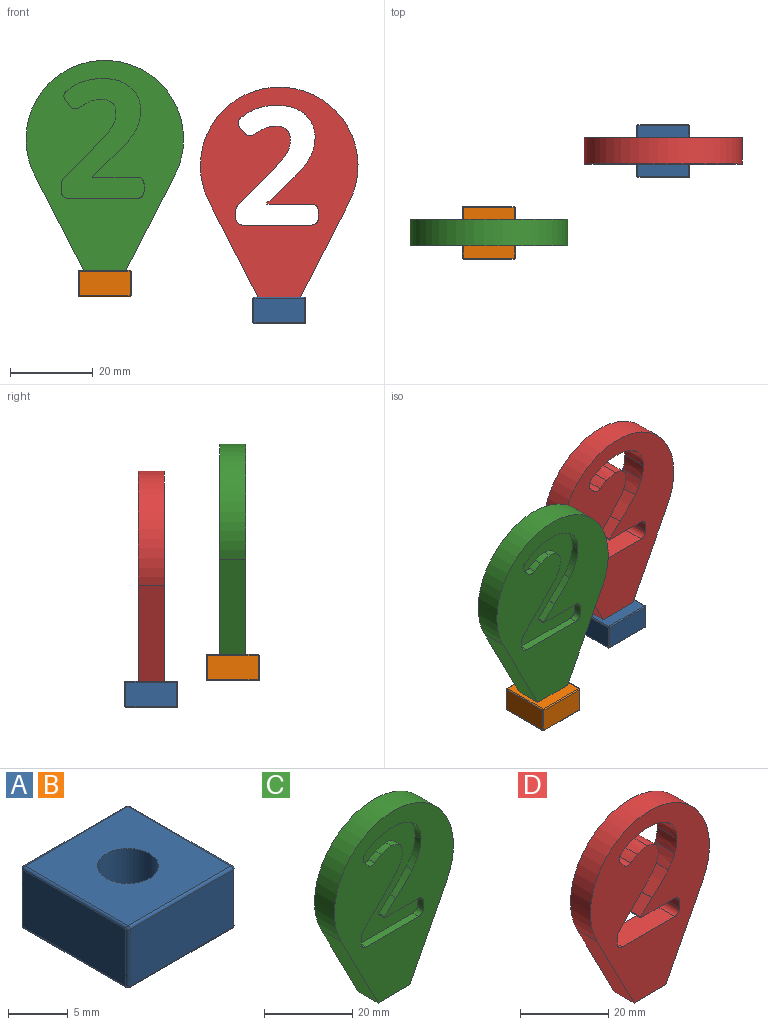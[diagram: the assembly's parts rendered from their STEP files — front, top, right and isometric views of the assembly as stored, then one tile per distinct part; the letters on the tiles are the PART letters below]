
ASSEMBLY  parts=4 mates=2
PART A: 28 faces, bbox 12.7x12.7x6.4 mm
  f0: plane 12.19x5.84mm, normal (-1,0,0), area 71.2mm2, adj f16,f21,f24,f27
  f1: plane 12.19x5.84mm, normal (0,-1,0), area 71.2mm2, adj f13,f22,f23,f27
  f2: plane 12.19x5.84mm, normal (1,0,0), area 71.2mm2, adj f8,f12,f13,f14
  f3: cylinder r=2.54mm len=5.08mm, axis (0,0,-1), area 60.8mm2, adj f5,f7
  f4: plane 12.19x5.84mm, normal (0,1,0), area 71.2mm2, adj f8,f11,f15,f16
  f5: plane 12.19x12.19mm, normal (0,0,1), area 128.4mm2, adj f3,f11,f12,f21,f22
  f6: plane 12.19x12.19mm, normal (0,0,-1), area 67.6mm2, adj f7,f14,f15,f23,f24
  f7: cone r=5.08mm half-angle=45deg, axis (0,0,-1), area 86mm2, adj f3,f6
  f8: cylinder r=0.25mm len=5.84mm, axis (0,0,-1), area 2.3mm2, adj f2,f4,f9,f10
  f9: sphere r=0.25mm, area 0.1mm2, adj f8,f11,f12
  f10: sphere r=0.25mm, area 0.1mm2, adj f8,f14,f15
  f11: cylinder r=0.25mm len=12.19mm, axis (1,0,0), area 4.9mm2, adj f4,f5,f9,f17
  f12: cylinder r=0.25mm len=12.19mm, axis (0,-1,0), area 4.9mm2, adj f2,f5,f9,f18
  f13: cylinder r=0.25mm len=5.84mm, axis (0,0,1), area 2.3mm2, adj f1,f2,f18,f19
  f14: cylinder r=0.25mm len=12.19mm, axis (0,1,0), area 4.9mm2, adj f2,f6,f10,f19
  f15: cylinder r=0.25mm len=12.19mm, axis (-1,0,0), area 4.9mm2, adj f4,f6,f10,f20
  f16: cylinder r=0.25mm len=5.84mm, axis (0,0,1), area 2.3mm2, adj f0,f4,f17,f20
  f17: sphere r=0.25mm, area 0.1mm2, adj f11,f16,f21
  f18: sphere r=0.25mm, area 0.1mm2, adj f12,f13,f22
  f19: sphere r=0.25mm, area 0.1mm2, adj f13,f14,f23
  f20: sphere r=0.25mm, area 0.1mm2, adj f15,f16,f24
  f21: cylinder r=0.25mm len=12.19mm, axis (0,1,0), area 4.9mm2, adj f0,f5,f17,f25
  f22: cylinder r=0.25mm len=12.19mm, axis (-1,0,0), area 4.9mm2, adj f1,f5,f18,f25
  f23: cylinder r=0.25mm len=12.19mm, axis (1,0,0), area 4.9mm2, adj f1,f6,f19,f26
  f24: cylinder r=0.25mm len=12.19mm, axis (0,-1,0), area 4.9mm2, adj f0,f6,f20,f26
  f25: sphere r=0.25mm, area 0.1mm2, adj f21,f22,f27
  f26: sphere r=0.25mm, area 0.1mm2, adj f23,f24,f27
  f27: cylinder r=0.25mm len=5.84mm, axis (0,0,-1), area 2.3mm2, adj f0,f1,f25,f26
PART B: same geometry as A
PART C: 70 faces, bbox 38.1x6.4x50.8 mm
  f0: plane 1.91x1.9mm, normal (-1,0,0), area 3.6mm2, adj f30,f31,f61,f68
  f1: plane 16.78x1.91mm, normal (0,0,1), area 32mm2, adj f24,f31,f61,f68
  f2: plane 1.96x1.91mm, normal (1,0,0), area 3.7mm2, adj f24,f25,f61,f68
  f3: plane 6.78x6.71mm, normal (0.71,0,-0.7), area 18.2mm2, adj f19,f25,f61,f68
  f4: extruded ~2.33x1.91mm, area 5.2mm2, adj f5,f19,f61,f68
  f5: extruded ~2.22x1.91mm, area 4.3mm2, adj f4,f6,f61,f68
  f6: extruded ~2.56x1.91mm, area 5.4mm2, adj f5,f7,f61,f68
  f7: extruded ~2.53x1.91mm, area 5.2mm2, adj f6,f8,f61,f68
  f8: extruded ~3.22x1.91mm, area 6.4mm2, adj f7,f20,f61,f68
  f9: plane 1.91x1.49mm, normal (0.76,0,0.65), area 3.7mm2, adj f26,f27,f61,f68
  f10: extruded ~3.03x1.91mm, area 6.2mm2, adj f11,f21,f61,f68
  f11: extruded ~3.67x1.91mm, area 7mm2, adj f10,f12,f61,f68
  f12: extruded ~4.72x1.91mm, area 9.3mm2, adj f11,f13,f61,f68
  f13: extruded ~3.18x2.73mm, area 8.1mm2, adj f12,f14,f61,f68
  f14: extruded ~4.02x1.91mm, area 8.1mm2, adj f13,f15,f61,f68
  f15: extruded ~3.7x1.91mm, area 7.2mm2, adj f14,f16,f61,f68
  f16: extruded ~3.54x2.15mm, area 7.9mm2, adj f15,f22,f61,f68
  f17: plane 3.67x3.45mm, normal (-0.69,0,0.73), area 9.6mm2, adj f23,f28,f61,f68
  f18: plane 10.85x1.91mm, normal (0,0,-1), area 20.7mm2, adj f23,f30,f61,f68
  f19: extruded ~4.52x4.16mm, area 11.7mm2, adj f3,f4,f61,f68
  f20: extruded ~2.1x1.91mm, area 4.7mm2, adj f8,f26,f61,f68
  f21: extruded ~2.22x1.91mm, area 5.1mm2, adj f10,f27,f61,f68
  f22: extruded ~5.17x5.12mm, area 13.9mm2, adj f16,f28,f61,f68
  f23: plane 1.91x0.27mm, normal (-1,0,0), area 0.5mm2, adj f17,f18,f61,f68
  f24: cylinder r=1.59mm len=1.91mm, axis (0,-1,0), area 4.8mm2, adj f1,f2,f61,f68
  f25: cylinder r=1.59mm len=1.91mm, axis (0,-1,0), area 2.4mm2, adj f2,f3,f61,f68
  f26: cylinder r=1.59mm len=2.14mm, axis (0,1,0), area 4.5mm2, adj f9,f20,f61,f68
  f27: cylinder r=1.59mm len=2.28mm, axis (0,1,0), area 4.9mm2, adj f9,f21,f61,f68
  f28: cylinder r=1.59mm len=1.91mm, axis (0,1,0), area 0mm2, adj f17,f22,f61,f68
  f29: cylinder r=1.59mm len=1.91mm, axis (0,1,0), area 0mm2, adj f55,f56,f60,f69
  f30: cylinder r=1.59mm len=1.91mm, axis (0,-1,0), area 4.8mm2, adj f0,f18,f61,f68
  f31: cylinder r=1.59mm len=1.91mm, axis (0,-1,0), area 4.8mm2, adj f0,f1,f61,f68
  f32: cylinder r=19.05mm len=38.1mm, axis (0,1,0), area 495.1mm2, adj f33,f59,f60,f61
  f33: plane 23.03x11.86mm, normal (-0.89,0,-0.46), area 164.5mm2, adj f32,f34,f60,f61
  f34: plane 10.16x6.35mm, normal (0,0,-1), area 64.5mm2, adj f33,f59,f60,f61
  f35: plane 1.91x1.9mm, normal (-1,0,0), area 3.6mm2, adj f60,f66,f67,f69
  f36: plane 16.78x1.91mm, normal (0,0,1), area 32mm2, adj f60,f62,f67,f69
  f37: plane 1.96x1.91mm, normal (1,0,0), area 3.7mm2, adj f60,f62,f63,f69
  f38: plane 6.78x6.71mm, normal (0.71,0,-0.7), area 18.2mm2, adj f39,f60,f63,f69
  f39: extruded ~4.52x4.16mm, area 11.7mm2, adj f38,f40,f60,f69
  f40: extruded ~2.33x1.91mm, area 5.2mm2, adj f39,f41,f60,f69
  f41: extruded ~2.22x1.91mm, area 4.3mm2, adj f40,f42,f60,f69
  f42: extruded ~2.56x1.91mm, area 5.4mm2, adj f41,f43,f60,f69
  f43: extruded ~2.53x1.91mm, area 5.2mm2, adj f42,f44,f60,f69
  f44: extruded ~3.22x1.91mm, area 6.4mm2, adj f43,f45,f60,f69
  f45: extruded ~2.1x1.91mm, area 4.7mm2, adj f44,f60,f64,f69
  f46: plane 1.91x1.49mm, normal (0.76,0,0.65), area 3.7mm2, adj f60,f64,f65,f69
  f47: extruded ~2.22x1.91mm, area 5.1mm2, adj f48,f60,f65,f69
  f48: extruded ~3.03x1.91mm, area 6.2mm2, adj f47,f49,f60,f69
  f49: extruded ~3.67x1.91mm, area 7mm2, adj f48,f50,f60,f69
  f50: extruded ~4.72x1.91mm, area 9.3mm2, adj f49,f51,f60,f69
  f51: extruded ~3.18x2.73mm, area 8.1mm2, adj f50,f52,f60,f69
  f52: extruded ~4.02x1.91mm, area 8.1mm2, adj f51,f53,f60,f69
  f53: extruded ~3.7x1.91mm, area 7.2mm2, adj f52,f54,f60,f69
  f54: extruded ~3.54x2.15mm, area 7.9mm2, adj f53,f55,f60,f69
  f55: extruded ~5.17x5.12mm, area 13.9mm2, adj f29,f54,f60,f69
  f56: plane 3.67x3.45mm, normal (-0.69,0,0.73), area 9.6mm2, adj f29,f57,f60,f69
  f57: plane 1.91x0.27mm, normal (-1,0,0), area 0.5mm2, adj f56,f58,f60,f69
  f58: plane 10.85x1.91mm, normal (0,0,-1), area 20.7mm2, adj f57,f60,f66,f69
  f59: plane 23.03x11.86mm, normal (0.89,0,-0.46), area 164.5mm2, adj f32,f34,f60,f61
  f60: plane 50.8x38.1mm, normal (0,-1,0), area 1096.6mm2, adj f29,f32,f33,f34,f35,f36,f37,f38
  f61: plane 50.8x38.1mm, normal (0,1,0), area 1096.6mm2, adj f0,f1,f2,f3,f4,f5,f6,f7
  f62: cylinder r=1.59mm len=1.91mm, axis (0,-1,0), area 4.8mm2, adj f36,f37,f60,f69
  f63: cylinder r=1.59mm len=1.91mm, axis (0,-1,0), area 2.4mm2, adj f37,f38,f60,f69
  f64: cylinder r=1.59mm len=2.14mm, axis (0,1,0), area 4.5mm2, adj f45,f46,f60,f69
  f65: cylinder r=1.59mm len=2.28mm, axis (0,1,0), area 4.9mm2, adj f46,f47,f60,f69
  f66: cylinder r=1.59mm len=1.91mm, axis (0,-1,0), area 4.8mm2, adj f35,f58,f60,f69
  f67: cylinder r=1.59mm len=1.91mm, axis (0,-1,0), area 4.8mm2, adj f35,f36,f60,f69
  f68: plane 28.95x19.95mm, normal (0,1,0), area 300.7mm2, adj f0,f1,f2,f3,f4,f5,f6,f7
  f69: plane 28.95x19.95mm, normal (0,-1,0), area 300.7mm2, adj f29,f35,f36,f37,f38,f39,f40,f41
PART D: 37 faces, bbox 38.1x6.4x50.8 mm
  f0: cylinder r=19.05mm len=38.1mm, axis (0,1,0), area 495.1mm2, adj f1,f27,f28,f29
  f1: plane 23.03x11.86mm, normal (-0.89,0,-0.46), area 164.5mm2, adj f0,f2,f28,f29
  f2: plane 10.16x6.35mm, normal (0,0,-1), area 64.5mm2, adj f1,f27,f28,f29
  f3: plane 6.35x1.9mm, normal (-1,0,0), area 12.1mm2, adj f28,f29,f35,f36
  f4: plane 16.78x6.35mm, normal (0,0,1), area 106.5mm2, adj f28,f29,f30,f36
  f5: plane 6.35x1.96mm, normal (1,0,0), area 12.4mm2, adj f28,f29,f30,f31
  f6: plane 6.78x6.71mm, normal (0.71,0,-0.7), area 60.5mm2, adj f7,f28,f29,f31
  f7: extruded ~6.35x4.52mm, area 39mm2, adj f6,f8,f28,f29
  f8: extruded ~6.35x2.33mm, area 17.4mm2, adj f7,f9,f28,f29
  f9: extruded ~6.35x2.22mm, area 14.5mm2, adj f8,f10,f28,f29
  f10: extruded ~6.35x2.56mm, area 17.9mm2, adj f9,f11,f28,f29
  f11: extruded ~6.35x2.53mm, area 17.3mm2, adj f10,f12,f28,f29
  f12: extruded ~6.35x3.22mm, area 21.2mm2, adj f11,f13,f28,f29
  f13: extruded ~6.35x2.1mm, area 15.6mm2, adj f12,f28,f29,f32
  f14: plane 6.35x1.49mm, normal (0.76,0,0.65), area 12.4mm2, adj f28,f29,f32,f33
  f15: extruded ~6.35x2.22mm, area 17mm2, adj f16,f28,f29,f33
  f16: extruded ~6.35x3.03mm, area 20.6mm2, adj f15,f17,f28,f29
  f17: extruded ~6.35x3.67mm, area 23.5mm2, adj f16,f18,f28,f29
  f18: extruded ~6.35x4.72mm, area 30.9mm2, adj f17,f19,f28,f29
  f19: extruded ~6.35x3.18mm, area 27mm2, adj f18,f20,f28,f29
  f20: extruded ~6.35x4.02mm, area 26.9mm2, adj f19,f21,f28,f29
  f21: extruded ~6.35x3.7mm, area 24.1mm2, adj f20,f22,f28,f29
  f22: extruded ~6.35x3.54mm, area 26.4mm2, adj f21,f23,f28,f29
  f23: extruded ~6.35x5.17mm, area 46.2mm2, adj f22,f28,f29,f34
  f24: plane 6.35x3.67mm, normal (-0.69,0,0.73), area 32mm2, adj f25,f28,f29,f34
  f25: plane 6.35x0.27mm, normal (-1,0,0), area 1.7mm2, adj f24,f26,f28,f29
  f26: plane 10.85x6.35mm, normal (0,0,-1), area 68.9mm2, adj f25,f28,f29,f35
  f27: plane 23.03x11.86mm, normal (0.89,0,-0.46), area 164.5mm2, adj f0,f2,f28,f29
  f28: plane 50.8x38.1mm, normal (0,-1,0), area 1096.6mm2, adj f0,f1,f2,f3,f4,f5,f6,f7
  f29: plane 50.8x38.1mm, normal (0,1,0), area 1096.6mm2, adj f0,f1,f2,f3,f4,f5,f6,f7
  f30: cylinder r=1.59mm len=6.35mm, axis (0,-1,0), area 15.8mm2, adj f4,f5,f28,f29
  f31: cylinder r=1.59mm len=6.35mm, axis (0,-1,0), area 7.9mm2, adj f5,f6,f28,f29
  f32: cylinder r=1.59mm len=6.35mm, axis (0,1,0), area 15mm2, adj f13,f14,f28,f29
  f33: cylinder r=1.59mm len=6.35mm, axis (0,1,0), area 16.2mm2, adj f14,f15,f28,f29
  f34: cylinder r=1.59mm len=6.35mm, axis (0,1,0), area 0.1mm2, adj f23,f24,f28,f29
  f35: cylinder r=1.59mm len=6.35mm, axis (0,-1,0), area 15.8mm2, adj f3,f26,f28,f29
  f36: cylinder r=1.59mm len=6.35mm, axis (0,-1,0), area 15.8mm2, adj f3,f4,f28,f29
PLACE A t=(42.95,21.35,-4.88)mm
PLACE B t=(0.79,1.59,1.59)mm
PLACE C t=(0.79,1.59,7.94)mm
PLACE D t=(-4.3,21.35,1.47)mm
MATE revolute D.f2 <-> A.f3  axis (0,0,-1) through (42.95,21.35,1.47)mm
MATE revolute C.f34 <-> B.f3  axis (0,0,-1) through (0.79,1.59,7.94)mm
